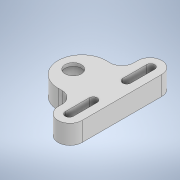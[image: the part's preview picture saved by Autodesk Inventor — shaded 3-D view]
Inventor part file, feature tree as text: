
AUTODESK INVENTOR PART (.ipt)
format: ipt  version: 2021.3 (Build 253353000, 353)  size: 193,536 bytes
history: native  units: mm
features: sketch x4, extrude x3, fillet x2, hole x1
ambient origin geometry x8: Origin, YZ Plane, XZ Plane, XY Plane, X Axis, Y Axis, Z Axis, Center Point
bodies: Body1 (feature_tree)
feature tree (10):
  extrude  "Extrusion3"  Depth=30.0mm
  extrude  "Extrusion5"  Depth=40.0mm
  extrude  "Extrusion6"  Depth=12.0mm TaperAngle=0.0deg
  fillet  "Rundung4"  Radius=5.1mm
  fillet  "Rundung5"  Radius=5.1mm
  hole  "Bohrung1"  [1 undecoded]
  sketch  "Skizze1"  dims[d0=65.0mm d1=30.0mm]
  sketch  "Skizze5"  dims[d2=15.0mm d3=40.0mm]
  sketch  "Skizze6"  dims[d6=25.0mm d45=12.0mm d46=0.0mm d52=5.1mm d53=5.1mm]
  sketch  "Skizze7"  dims[d54=15.0mm d55=15.0mm d56=7.0mm d58=7.0mm d59=15.0mm d60=7.5mm d61=0.0mm d62=0.0mm d63=10.0mm d64=10.0mm d65=15.0mm d66=15.0mm d67=7.0mm d68=7.5mm d69=7.5mm d70=7.0mm d71=5.0mm d72=0.0mm d74=7.5mm d75=15.0mm d76=36.0mm d77=32.5mm d78=30.5mm d79=10.2mm d80=20.0mm d81=17.0mm d82=10.0mm d83=90.0deg d84=8.0mm d85=20.594885mm]
note: 1 required parameter value undecoded (feature->parameter linkage not recoverable at this tier; creation-order binding heuristic only, values carry confidence <= 0.55)
